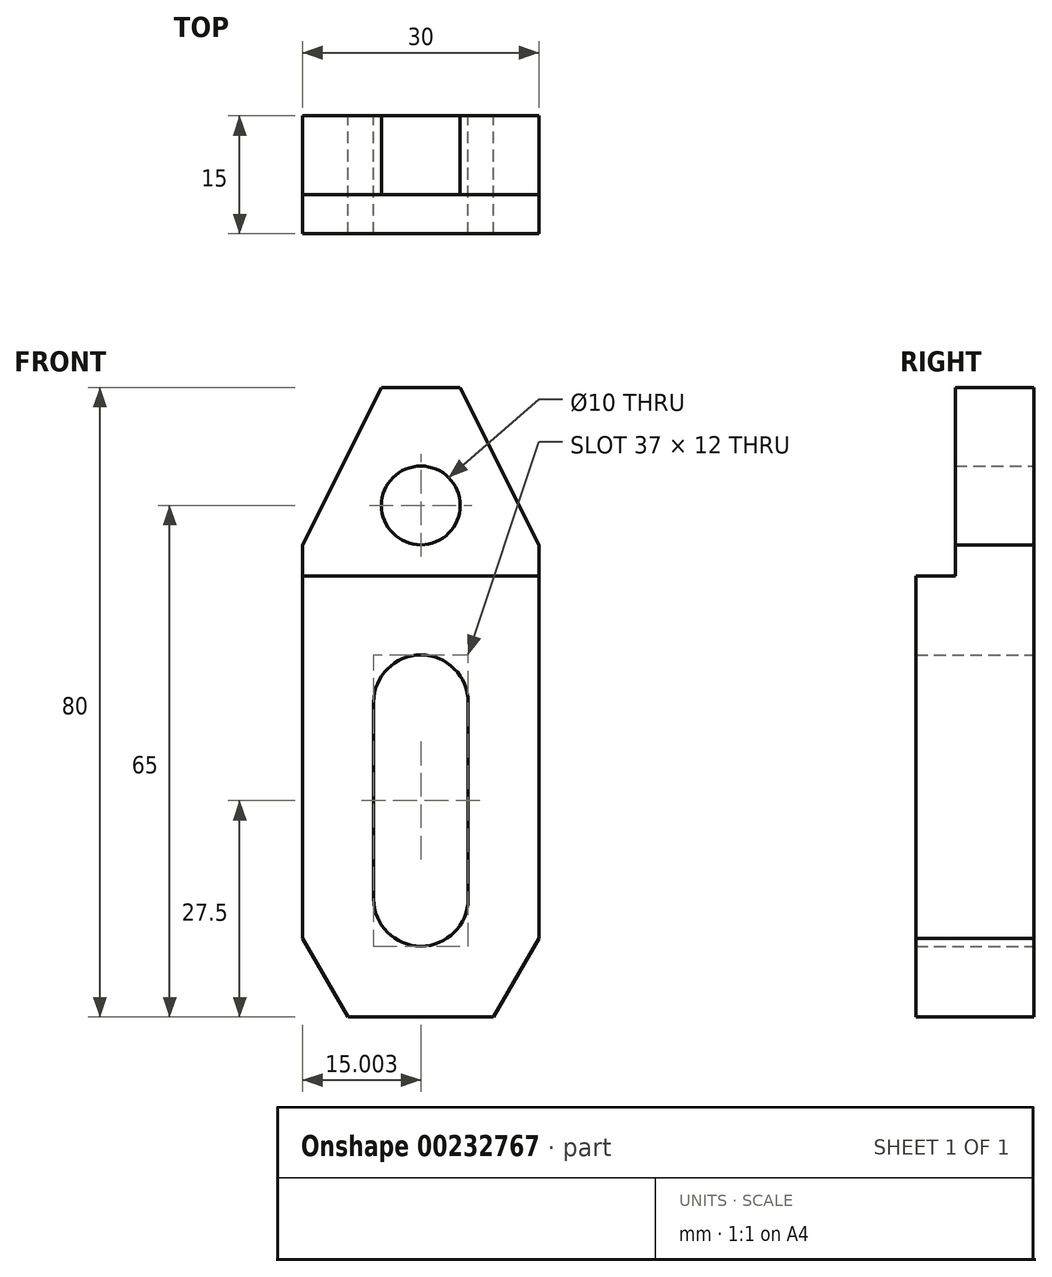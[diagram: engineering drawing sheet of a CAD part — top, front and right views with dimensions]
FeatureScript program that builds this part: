
annotation { "Feature Type Name" : "Feature", "Feature Type Description" : "" }
export const myFeature = defineFeature(function(context is Context, id is Id, definition is map)
    precondition{}
    {
        {
            var Q0;
            Q0=qCreatedBy(makeId("Front.planeOp"),FACE);
            var sketch = newSketch(context, id + "F0", { "sketchPlane" : qUnion([Q0])});
            skLineSegment(sketch, "E0", {"start": v(-22.18, 16) * mm, "end": v(7.82, 16) * mm});
            skLineSegment(sketch, "E1", {"start": v(7.82, 16) * mm, "end": v(7.82, -30) * mm});
            skLineSegment(sketch, "E2", {"start": v(7.82, -30) * mm, "end": v(2.05, -40) * mm});
            skLineSegment(sketch, "E3", {"start": v(-22.18, 16) * mm, "end": v(-22.18, 20) * mm});
            skLineSegment(sketch, "E4", {"start": v(7.82, 16) * mm, "end": v(7.82, 20) * mm});
            skLineSegment(sketch, "E5", {"start": v(-22.18, 20) * mm, "end": v(-12.18, 40) * mm});
            skLineSegment(sketch, "E6", {"start": v(-12.18, 40) * mm, "end": v(-2.18, 40) * mm});
            skLineSegment(sketch, "E7", {"start": v(-2.18, 40) * mm, "end": v(7.82, 20) * mm});
            skLineSegment(sketch, "E8", {"start": v(2.05, -40) * mm, "end": v(-16.4, -40) * mm});
            skLineSegment(sketch, "E9", {"start": v(-16.4, -40) * mm, "end": v(-22.18, -30) * mm});
            skLineSegment(sketch, "E10", {"start": v(-22.18, -30) * mm, "end": v(-22.18, 16) * mm});
            skPoint(sketch, "E11", {"position": v(-7.18, -40) * mm});
            skArc(sketch, "E12", {"start": v(-13.18, -25) * mm, "mid": v(-7.18, -31) * mm, "end": v(-1.18, -25) * mm});
            skArc(sketch, "E13", {"start": v(-1.18, 0) * mm, "mid": v(-7.18, 6) * mm, "end": v(-13.18, 0) * mm});
            skCircle(sketch, "E14", {"center": v(-7.18, 25) * mm, "radius": 5 * mm});
            skLineSegment(sketch, "E15", {"start": v(-13.18, 0) * mm, "end": v(-13.18, -25) * mm});
            skLineSegment(sketch, "E16", {"start": v(-1.18, -25) * mm, "end": v(-1.18, 0) * mm});
            skSolve(sketch);
        }
        {
            var Q0;
            Q0=makeQuery(id+"F0.imprint","IMPRINT",FACE,{"disambiguationData":[TD([[makeQuery(id+"F0.imprint","IMPRINT",EDGE,{"derivedFrom":sQuery(id+"F0.wireOp",EDGE,"E0")}),-1.0]])]});
            extrude(context, id + "F1", {"entities" : qUnion([Q0]), "depth" : 15 * mm});
        }
        {
            var Q0;
            Q0=makeQuery(id+"F0.imprint","IMPRINT",FACE,{"disambiguationData":[TD([[makeQuery(id+"F0.imprint","IMPRINT",EDGE,{"derivedFrom":sQuery(id+"F0.wireOp",EDGE,"E0")}),1.0]])]});
            extrude(context, id + "F2", {"entities" : qUnion([Q0]), "operationType" : NewBodyOperationType.ADD, "depth" : 10 * mm});
        }
    });
